FCSTD DOCUMENT  (FreeCAD 0.18R16093 +53 (Git))
Label: base
License: All rights reserved
LicenseURL: http://en.wikipedia.org/wiki/All_rights_reserved
objects: Sketcher::SketchObject×1
note: 1 computed .brp shape members not serialized (recipe doc carries the construction recipe); baked Part::Feature solids carry a one-line shape summary decoded from their .brp

FEATURE [Sketcher::SketchObject] Sketch
  sketch-geometry (15):
    g0: Circle CenterX=0 CenterY=0 CenterZ=0 NormalX=0 NormalY=0 NormalZ=1 AngleXU=0 Radius=100
    g1: Circle CenterX=0 CenterY=0 CenterZ=0 NormalX=0 NormalY=0 NormalZ=1 AngleXU=0 Radius=10
    g2: Circle CenterX=13 CenterY=13 CenterZ=0 NormalX=0 NormalY=0 NormalZ=1 AngleXU=0 Radius=2
    g3: Circle CenterX=15.5 CenterY=15.5 CenterZ=0 NormalX=0 NormalY=0 NormalZ=1 AngleXU=0 Radius=2
    g4: Circle CenterX=23.57 CenterY=23.57 CenterZ=0 NormalX=0 NormalY=0 NormalZ=1 AngleXU=0 Radius=2.6
    g5: GeomPoint X=13.6949 Y=14.4226 Z=0
    g6: Circle CenterX=-23.57 CenterY=23.57 CenterZ=0 NormalX=0 NormalY=0 NormalZ=1 AngleXU=0 Radius=2.6
    g7: Circle CenterX=-15.5 CenterY=15.5 CenterZ=0 NormalX=0 NormalY=0 NormalZ=1 AngleXU=0 Radius=2
    g8: Circle CenterX=-13 CenterY=13 CenterZ=0 NormalX=0 NormalY=0 NormalZ=1 AngleXU=0 Radius=2
    g9: Circle CenterX=23.57 CenterY=-23.57 CenterZ=0 NormalX=0 NormalY=0 NormalZ=1 AngleXU=0 Radius=2.6
    g10: Circle CenterX=15.5 CenterY=-15.5 CenterZ=0 NormalX=0 NormalY=0 NormalZ=1 AngleXU=0 Radius=2
    g11: Circle CenterX=13 CenterY=-13 CenterZ=0 NormalX=0 NormalY=0 NormalZ=1 AngleXU=0 Radius=2
    g12: Circle CenterX=-13 CenterY=-13 CenterZ=0 NormalX=0 NormalY=0 NormalZ=1 AngleXU=0 Radius=2
    g13: Circle CenterX=-15.5 CenterY=-15.5 CenterZ=0 NormalX=0 NormalY=0 NormalZ=1 AngleXU=0 Radius=2
    g14: Circle CenterX=-23.57 CenterY=-23.57 CenterZ=0 NormalX=0 NormalY=0 NormalZ=1 AngleXU=0 Radius=2.6
  constraints (22):
    c: Radius(g0) = 100
    c: Coincident(g0,g-1)
    c: Radius(g1) = 10
    c: Coincident(g1,g0)
    c: Radius(g4) = 2.6
    c: Radius(g3) = 2
    c: Radius(g2) = 2
    c: DistanceX(g-1,g2) = 13
    c: DistanceY(g-1,g2) = 13
    c: DistanceX(g3) = 15.5
    c: DistanceY(g-1,g3) = 15.5
    c: DistanceX(g-1,g4) = 23.57
    c: DistanceY(g4) = 23.57
    c: Radius(g6) = 2.6
    c: Radius(g7) = 2
    c: Radius(g8) = 2
    c: Radius(g9) = 2.6
    c: Radius(g10) = 2
    c: Radius(g11) = 2
    c: Radius(g14) = 2.6
    c: Radius(g13) = 2
    c: Radius(g12) = 2
